# Revit family: Q90.195.xxx_with 3 shelves_4+6 drawers_RV15
name_source: partatom
category: Möbelsysteme
revit_build: Autodesk Revit 2015 (Build: 20140606_1530(x64)
units: mm (PartAtom-declared; Revit-internal decimal feet)

## types (27) — shared parameters
Beschreibung = GS-tested safety storage cabinets for unrestricted storage of flammable hazardous materials in work areas in accordance with EN 14470-1 and TRGS 510 with a fire resistance of 90 (Type 90)
Cabinet colour = RAL 7016 Anthracite grey
Cabinet depth = 615 mm  [stored 2.01772 ft]
Cabinet height = 1954 mm
Diff. pressure (Air change 10 times) = 5.0 Pa
Hersteller = asecos GmbH
Price information = Price from fall 2017
Price information 2 = Prices are ex works and without taxes and shipping
Product video = https://www.youtube.com
URL = https://www.asecos.com
zero-valued in all types: Sticker position rb

## per-type parameters (varying)
- Q90.195.060 with 3 shelves, warning yellow: 1200 mm 3 shelves=Nein; 1200 mm 4 drawers=Nein; 1200 mm 6 drawers=Nein; 600 mm 3 shelves=Ja; 600 mm 4 drawers=Nein; 600 mm 6 drawers=Nein; 900 mm 3 shelves=Nein; 900 mm 4 drawers=Nein; 900 mm 6 drawers=Nein; Air change 10 times=1.1 L/s; Air duct distance=145 mm  [stored 0.475722 ft]; Bestellnummer DACH=30072-040-30076; Cabinet width=600 mm; Distributed load=8.77 kN/m²; Door colour=RAL 1004 warning yellow; Door width=512 mm  [stored 1.67979 ft]; Double door=Nein; Handle position=514 mm; Kosten=2410 $; Modell=Q90.195.060 with 3 shelves; Order No. Global=30072-040-33407; Single door=Ja; Sticker position lb=269 mm; Sticker position ls=0 mm  [stored 0 ft]; Typenbild=30072-040.jpg
- Q90.195.060 with 3 shelves, light grey: 1200 mm 3 shelves=Nein; 1200 mm 4 drawers=Nein; 1200 mm 6 drawers=Nein; 600 mm 3 shelves=Ja; 600 mm 4 drawers=Nein; 600 mm 6 drawers=Nein; 900 mm 3 shelves=Nein; 900 mm 4 drawers=Nein; 900 mm 6 drawers=Nein; Air change 10 times=1.1 L/s; Air duct distance=145 mm  [stored 0.475722 ft]; Bestellnummer DACH=30072-041-30076; Cabinet width=600 mm; Distributed load=8.77 kN/m²; Door colour=RAL 7035 Light grey; Door width=512 mm  [stored 1.67979 ft]; Double door=Nein; Handle position=514 mm; Kosten=2410 $; Modell=Q90.195.060 with 3 shelves; Order No. Global=30072-041-33600; Single door=Ja; Sticker position lb=269 mm; Sticker position ls=0 mm  [stored 0 ft]; Typenbild=30072-041.jpg
- Q90.195.060 with 3 shelves, pure white: 1200 mm 3 shelves=Nein; 1200 mm 4 drawers=Nein; 1200 mm 6 drawers=Nein; 600 mm 3 shelves=Ja; 600 mm 4 drawers=Nein; 600 mm 6 drawers=Nein; 900 mm 3 shelves=Nein; 900 mm 4 drawers=Nein; 900 mm 6 drawers=Nein; Air change 10 times=1.1 L/s; Air duct distance=145 mm  [stored 0.475722 ft]; Bestellnummer DACH=30072-050-30076; Cabinet width=600 mm; Distributed load=8.77 kN/m²; Door colour=RAL 9010 Pure white; Door width=512 mm  [stored 1.67979 ft]; Double door=Nein; Handle position=514 mm; Kosten=2410 $; Modell=Q90.195.060 with 3 shelves; Order No. Global=30072-050-33407; Single door=Ja; Sticker position lb=269 mm; Sticker position ls=0 mm  [stored 0 ft]; Typenbild=30072-050.jpg
- Q90.195.060 with 4 drawers, warning yellow: 1200 mm 3 shelves=Nein; 1200 mm 4 drawers=Nein; 1200 mm 6 drawers=Nein; 600 mm 3 shelves=Nein; 600 mm 4 drawers=Ja; 600 mm 6 drawers=Nein; 900 mm 3 shelves=Nein; 900 mm 4 drawers=Nein; 900 mm 6 drawers=Nein; Air change 10 times=1.1 L/s; Air duct distance=145 mm  [stored 0.475722 ft]; Bestellnummer DACH=30072-040-30088; Cabinet width=600 mm; Distributed load=8.77 kN/m²; Door colour=RAL 1004 warning yellow; Door width=512 mm  [stored 1.67979 ft]; Double door=Nein; Handle position=514 mm; Kosten=2720 $; Modell=Q90.195.060 with 4 drawers; Order No. Global=30072-040-33608; Single door=Ja; Sticker position lb=269 mm; Sticker position ls=0 mm  [stored 0 ft]; Typenbild=30072-040.jpg
- Q90.195.060 with 4 drawers, light grey: 1200 mm 3 shelves=Nein; 1200 mm 4 drawers=Nein; 1200 mm 6 drawers=Nein; 600 mm 3 shelves=Nein; 600 mm 4 drawers=Ja; 600 mm 6 drawers=Nein; 900 mm 3 shelves=Nein; 900 mm 4 drawers=Nein; 900 mm 6 drawers=Nein; Air change 10 times=1.1 L/s; Air duct distance=145 mm  [stored 0.475722 ft]; Bestellnummer DACH=30072-041-30088; Cabinet width=600 mm; Distributed load=8.77 kN/m²; Door colour=RAL 7035 Light grey; Door width=512 mm  [stored 1.67979 ft]; Double door=Nein; Handle position=514 mm; Kosten=2720 $; Modell=Q90.195.060 with 4 drawers; Order No. Global=30072-041-333608; Single door=Ja; Sticker position lb=269 mm; Sticker position ls=0 mm  [stored 0 ft]; Typenbild=30072-041.jpg
- Q90.195.060 with 4 drawers, pure white: 1200 mm 3 shelves=Nein; 1200 mm 4 drawers=Nein; 1200 mm 6 drawers=Nein; 600 mm 3 shelves=Nein; 600 mm 4 drawers=Ja; 600 mm 6 drawers=Nein; 900 mm 3 shelves=Nein; 900 mm 4 drawers=Nein; 900 mm 6 drawers=Nein; Air change 10 times=1.1 L/s; Air duct distance=145 mm  [stored 0.475722 ft]; Bestellnummer DACH=30072-050-30088; Cabinet width=600 mm; Distributed load=8.77 kN/m²; Door colour=RAL 9010 Pure white; Door width=512 mm  [stored 1.67979 ft]; Double door=Nein; Handle position=514 mm; Kosten=2720 $; Modell=Q90.195.060 with 4 drawers; Order No. Global=30072-050-33608; Single door=Ja; Sticker position lb=269 mm; Sticker position ls=0 mm  [stored 0 ft]; Typenbild=30072-050.jpg
- Q90.195.060 with 6 drawers, warning yellow: 1200 mm 3 shelves=Nein; 1200 mm 4 drawers=Nein; 1200 mm 6 drawers=Nein; 600 mm 3 shelves=Nein; 600 mm 4 drawers=Nein; 600 mm 6 drawers=Ja; 900 mm 3 shelves=Nein; 900 mm 4 drawers=Nein; 900 mm 6 drawers=Nein; Air change 10 times=1.1 L/s; Air duct distance=145 mm  [stored 0.475722 ft]; Bestellnummer DACH=30072-040-30090; Cabinet width=600 mm; Distributed load=8.77 kN/m²; Door colour=RAL 1004 warning yellow; Door width=512 mm  [stored 1.67979 ft]; Double door=Nein; Handle position=514 mm; Kosten=2960 $; Modell=Q90.195.060 with 6 drawers; Order No. Global=30072-040-33610; Single door=Ja; Sticker position lb=269 mm; Sticker position ls=0 mm  [stored 0 ft]; Typenbild=30072-040.jpg
- Q90.195.060 with 6 drawers, light grey: 1200 mm 3 shelves=Nein; 1200 mm 4 drawers=Nein; 1200 mm 6 drawers=Nein; 600 mm 3 shelves=Nein; 600 mm 4 drawers=Nein; 600 mm 6 drawers=Ja; 900 mm 3 shelves=Nein; 900 mm 4 drawers=Nein; 900 mm 6 drawers=Nein; Air change 10 times=1.1 L/s; Air duct distance=145 mm  [stored 0.475722 ft]; Bestellnummer DACH=30072-041-30090; Cabinet width=600 mm; Distributed load=8.77 kN/m²; Door colour=RAL 7035 Light grey; Door width=512 mm  [stored 1.67979 ft]; Double door=Nein; Handle position=514 mm; Kosten=2960 $; Modell=Q90.195.060 with 6 drawers; Order No. Global=30072-041-33610; Single door=Ja; Sticker position lb=269 mm; Sticker position ls=0 mm  [stored 0 ft]; Typenbild=30072-041.jpg
- Q90.195.060 with 6 drawers, pure white: 1200 mm 3 shelves=Nein; 1200 mm 4 drawers=Nein; 1200 mm 6 drawers=Nein; 600 mm 3 shelves=Nein; 600 mm 4 drawers=Nein; 600 mm 6 drawers=Ja; 900 mm 3 shelves=Nein; 900 mm 4 drawers=Nein; 900 mm 6 drawers=Nein; Air change 10 times=1.1 L/s; Air duct distance=145 mm  [stored 0.475722 ft]; Bestellnummer DACH=30072-050-30090; Cabinet width=600 mm; Distributed load=8.77 kN/m²; Door colour=RAL 9010 Pure white; Door width=512 mm  [stored 1.67979 ft]; Double door=Nein; Handle position=514 mm; Kosten=2960 $; Modell=Q90.195.060 with 6 drawers; Order No. Global=30072-050-33610; Single door=Ja; Sticker position lb=269 mm; Sticker position ls=0 mm  [stored 0 ft]; Typenbild=30072-050.jpg
- Q90.195.090 with 3 shelves, warning yellow: 1200 mm 3 shelves=Nein; 1200 mm 4 drawers=Nein; 1200 mm 6 drawers=Nein; 600 mm 3 shelves=Nein; 600 mm 4 drawers=Nein; 600 mm 6 drawers=Nein; 900 mm 3 shelves=Ja; 900 mm 4 drawers=Nein; 900 mm 6 drawers=Nein; Air change 10 times=1.7 L/s; Air duct distance=292 mm  [stored 0.958005 ft]; Bestellnummer DACH=30041-040-30043; Cabinet width=894 mm; Distributed load=6.41 kN/m²; Door colour=RAL 1004 warning yellow; Door width=399 mm; Double door=Ja; Handle position=401 mm; Kosten=3000 $; Modell=Q90.195.090 with 3 shelves; Order No. Global=30041-040-33622; Single door=Nein; Sticker position lb=156 mm; Sticker position ls=300 mm; Typenbild=30041-040.jpg
- Q90.195.090 with 3 shelves, light grey: 1200 mm 3 shelves=Nein; 1200 mm 4 drawers=Nein; 1200 mm 6 drawers=Nein; 600 mm 3 shelves=Nein; 600 mm 4 drawers=Nein; 600 mm 6 drawers=Nein; 900 mm 3 shelves=Ja; 900 mm 4 drawers=Nein; 900 mm 6 drawers=Nein; Air change 10 times=1.7 L/s; Air duct distance=292 mm  [stored 0.958005 ft]; Bestellnummer DACH=30041-041-30043; Cabinet width=894 mm; Distributed load=6.41 kN/m²; Door colour=RAL 7035 Light grey; Door width=399 mm; Double door=Ja; Handle position=401 mm; Kosten=3000 $; Modell=Q90.195.090 with 3 shelves; Order No. Global=30041-041-33622; Single door=Nein; Sticker position lb=156 mm; Sticker position ls=300 mm; Typenbild=30041-041.jpg
- Q90.195.090 with 3 shelves, pure white: 1200 mm 3 shelves=Nein; 1200 mm 4 drawers=Nein; 1200 mm 6 drawers=Nein; 600 mm 3 shelves=Nein; 600 mm 4 drawers=Nein; 600 mm 6 drawers=Nein; 900 mm 3 shelves=Ja; 900 mm 4 drawers=Nein; 900 mm 6 drawers=Nein; Air change 10 times=1.7 L/s; Air duct distance=292 mm  [stored 0.958005 ft]; Bestellnummer DACH=30041-050-30043; Cabinet width=894 mm; Distributed load=6.41 kN/m²; Door colour=RAL 9010 Pure white; Door width=399 mm; Double door=Ja; Handle position=401 mm; Kosten=3000 $; Modell=Q90.195.090 with 3 shelves; Order No. Global=30041-050-33622; Single door=Nein; Sticker position lb=156 mm; Sticker position ls=300 mm; Typenbild=30041-050.jpg
- Q90.195.090 with 4 drawers, warning yellow: 1200 mm 3 shelves=Nein; 1200 mm 4 drawers=Nein; 1200 mm 6 drawers=Nein; 600 mm 3 shelves=Nein; 600 mm 4 drawers=Nein; 600 mm 6 drawers=Nein; 900 mm 3 shelves=Nein; 900 mm 4 drawers=Ja; 900 mm 6 drawers=Nein; Air change 10 times=1.7 L/s; Air duct distance=292 mm  [stored 0.958005 ft]; Bestellnummer DACH=30041-40-30053; Cabinet width=894 mm; Distributed load=6.41 kN/m²; Door colour=RAL 1004 warning yellow; Door width=399 mm; Double door=Ja; Handle position=401 mm; Kosten=3560 $; Modell=Q90.195.090 with 4 drawers; Order No. Global=30041-40-33627; Single door=Nein; Sticker position lb=156 mm; Sticker position ls=300 mm; Typenbild=30041-040.jpg
- Q90.195.090 with 4 drawers, light grey: 1200 mm 3 shelves=Nein; 1200 mm 4 drawers=Nein; 1200 mm 6 drawers=Nein; 600 mm 3 shelves=Nein; 600 mm 4 drawers=Nein; 600 mm 6 drawers=Nein; 900 mm 3 shelves=Nein; 900 mm 4 drawers=Ja; 900 mm 6 drawers=Nein; Air change 10 times=1.7 L/s; Air duct distance=292 mm  [stored 0.958005 ft]; Bestellnummer DACH=30041-41-30053; Cabinet width=894 mm; Distributed load=6.41 kN/m²; Door colour=RAL 7035 Light grey; Door width=399 mm; Double door=Ja; Handle position=401 mm; Kosten=3560 $; Modell=Q90.195.090 with 4 drawers; Order No. Global=30041-41-33627; Single door=Nein; Sticker position lb=156 mm; Sticker position ls=300 mm; Typenbild=30041-041.jpg
- Q90.195.090 with 4 drawers, pure white: 1200 mm 3 shelves=Nein; 1200 mm 4 drawers=Nein; 1200 mm 6 drawers=Nein; 600 mm 3 shelves=Nein; 600 mm 4 drawers=Nein; 600 mm 6 drawers=Nein; 900 mm 3 shelves=Nein; 900 mm 4 drawers=Ja; 900 mm 6 drawers=Nein; Air change 10 times=1.7 L/s; Air duct distance=292 mm  [stored 0.958005 ft]; Bestellnummer DACH=30041-050-30053; Cabinet width=894 mm; Distributed load=6.41 kN/m²; Door colour=RAL 9010 Pure white; Door width=399 mm; Double door=Ja; Handle position=401 mm; Kosten=3560 $; Modell=Q90.195.090 with 4 drawers; Order No. Global=30041-050-33627; Single door=Nein; Sticker position lb=156 mm; Sticker position ls=300 mm; Typenbild=30041-050.jpg
- Q90.195.090 with 6 drawers, warning yellow: 1200 mm 3 shelves=Nein; 1200 mm 4 drawers=Nein; 1200 mm 6 drawers=Nein; 600 mm 3 shelves=Nein; 600 mm 4 drawers=Nein; 600 mm 6 drawers=Nein; 900 mm 3 shelves=Nein; 900 mm 4 drawers=Nein; 900 mm 6 drawers=Ja; Air change 10 times=1.7 L/s; Air duct distance=292 mm  [stored 0.958005 ft]; Bestellnummer DACH=30041-040-30055; Cabinet width=894 mm; Distributed load=6.41 kN/m²; Door colour=RAL 1004 warning yellow; Door width=399 mm; Double door=Ja; Handle position=401 mm; Kosten=3940 $; Modell=Q90.195.090 with 6 drawers; Order No. Global=30041-040-33629; Single door=Nein; Sticker position lb=156 mm; Sticker position ls=300 mm; Typenbild=30041-040.jpg
- Q90.195.090 with 6 drawers, light grey: 1200 mm 3 shelves=Nein; 1200 mm 4 drawers=Nein; 1200 mm 6 drawers=Nein; 600 mm 3 shelves=Nein; 600 mm 4 drawers=Nein; 600 mm 6 drawers=Nein; 900 mm 3 shelves=Nein; 900 mm 4 drawers=Nein; 900 mm 6 drawers=Ja; Air change 10 times=1.7 L/s; Air duct distance=292 mm  [stored 0.958005 ft]; Bestellnummer DACH=30041-041-30055; Cabinet width=894 mm; Distributed load=6.41 kN/m²; Door colour=RAL 7035 Light grey; Door width=399 mm; Double door=Ja; Handle position=401 mm; Kosten=3940 $; Modell=Q90.195.090 with 6 drawers; Order No. Global=30041-041-33629; Single door=Nein; Sticker position lb=156 mm; Sticker position ls=300 mm; Typenbild=30041-041.jpg
- Q90.195.090 with 6 drawers, pure white: 1200 mm 3 shelves=Nein; 1200 mm 4 drawers=Nein; 1200 mm 6 drawers=Nein; 600 mm 3 shelves=Nein; 600 mm 4 drawers=Nein; 600 mm 6 drawers=Nein; 900 mm 3 shelves=Nein; 900 mm 4 drawers=Nein; 900 mm 6 drawers=Ja; Air change 10 times=1.7 L/s; Air duct distance=292 mm  [stored 0.958005 ft]; Bestellnummer DACH=30041-050-30055; Cabinet width=894 mm; Distributed load=6.41 kN/m²; Door colour=RAL 9010 Pure white; Door width=399 mm; Double door=Ja; Handle position=401 mm; Kosten=3940 $; Modell=Q90.195.090 with 6 drawers; Order No. Global=30041-050-33629; Single door=Nein; Sticker position lb=156 mm; Sticker position ls=300 mm; Typenbild=30041-050.jpg
- Q90.195.120 with 3 shelves, warning yellow: 1200 mm 3 shelves=Ja; 1200 mm 4 drawers=Nein; 1200 mm 6 drawers=Nein; 600 mm 3 shelves=Nein; 600 mm 4 drawers=Nein; 600 mm 6 drawers=Nein; 900 mm 3 shelves=Nein; 900 mm 4 drawers=Nein; 900 mm 6 drawers=Nein; Air change 10 times=2.5 L/s; Air duct distance=442 mm  [stored 1.45013 ft]; Bestellnummer DACH=30001-050-30003; Cabinet width=1194 mm; Distributed load=4.16 kN/m²; Door colour=RAL 1004 warning yellow; Door width=549 mm; Double door=Ja; Handle position=551 mm; Kosten=3340 $; Modell=Q90.195.120 with 3 shelves; Order No. Global=30001-050-33635; Single door=Nein; Sticker position lb=156 mm; Sticker position ls=450 mm  [stored 1.47638 ft]; Typenbild=30001-040.jpg
- Q90.195.120 with 3 shelves, light grey: 1200 mm 3 shelves=Ja; 1200 mm 4 drawers=Nein; 1200 mm 6 drawers=Nein; 600 mm 3 shelves=Nein; 600 mm 4 drawers=Nein; 600 mm 6 drawers=Nein; 900 mm 3 shelves=Nein; 900 mm 4 drawers=Nein; 900 mm 6 drawers=Nein; Air change 10 times=2.5 L/s; Air duct distance=442 mm  [stored 1.45013 ft]; Bestellnummer DACH=30001-041-30003; Cabinet width=1194 mm; Distributed load=4.16 kN/m²; Door colour=RAL 7035 Light grey; Door width=549 mm; Double door=Ja; Handle position=551 mm; Kosten=3340 $; Modell=Q90.195.120 with 3 shelves; Order No. Global=30001-041-33635; Single door=Nein; Sticker position lb=156 mm; Sticker position ls=450 mm  [stored 1.47638 ft]; Typenbild=30001-041.jpg
- Q90.195.120 with 3 shelves, pure white: 1200 mm 3 shelves=Ja; 1200 mm 4 drawers=Nein; 1200 mm 6 drawers=Nein; 600 mm 3 shelves=Nein; 600 mm 4 drawers=Nein; 600 mm 6 drawers=Nein; 900 mm 3 shelves=Nein; 900 mm 4 drawers=Nein; 900 mm 6 drawers=Nein; Air change 10 times=2.5 L/s; Air duct distance=442 mm  [stored 1.45013 ft]; Bestellnummer DACH=30001-050-30003; Cabinet width=1194 mm; Distributed load=4.16 kN/m²; Door colour=RAL 9010 Pure white; Door width=549 mm; Double door=Ja; Handle position=551 mm; Kosten=3340 $; Modell=Q90.195.120 with 3 shelves; Order No. Global=30001-050-33635; Single door=Nein; Sticker position lb=156 mm; Sticker position ls=450 mm  [stored 1.47638 ft]; Typenbild=30001-050.jpg
- Q90.195.120 with 4 drawers, warning yellow: 1200 mm 3 shelves=Nein; 1200 mm 4 drawers=Ja; 1200 mm 6 drawers=Nein; 600 mm 3 shelves=Nein; 600 mm 4 drawers=Nein; 600 mm 6 drawers=Nein; 900 mm 3 shelves=Nein; 900 mm 4 drawers=Nein; 900 mm 6 drawers=Nein; Air change 10 times=2.5 L/s; Air duct distance=442 mm  [stored 1.45013 ft]; Bestellnummer DACH=30001-040-30015; Cabinet width=1194 mm; Distributed load=4.16 kN/m²; Door colour=RAL 1004 warning yellow; Door width=549 mm; Double door=Ja; Handle position=551 mm; Kosten=3670 $; Modell=Q90.195.120 with 4 drawers; Order No. Global=30001-040-33647; Single door=Nein; Sticker position lb=156 mm; Sticker position ls=450 mm  [stored 1.47638 ft]; Typenbild=30001-040.jpg
- Q90.195.120 with 4 drawers, light grey: 1200 mm 3 shelves=Nein; 1200 mm 4 drawers=Ja; 1200 mm 6 drawers=Nein; 600 mm 3 shelves=Nein; 600 mm 4 drawers=Nein; 600 mm 6 drawers=Nein; 900 mm 3 shelves=Nein; 900 mm 4 drawers=Nein; 900 mm 6 drawers=Nein; Air change 10 times=2.5 L/s; Air duct distance=442 mm  [stored 1.45013 ft]; Bestellnummer DACH=30001-041-30015; Cabinet width=1194 mm; Distributed load=4.16 kN/m²; Door colour=RAL 7035 Light grey; Door width=549 mm; Double door=Ja; Handle position=551 mm; Kosten=3670 $; Modell=Q90.195.120 with 4 drawers; Order No. Global=30001-041-33647; Single door=Nein; Sticker position lb=156 mm; Sticker position ls=450 mm  [stored 1.47638 ft]; Typenbild=30001-041.jpg
- Q90.195.120 with 4 drawers, pure white: 1200 mm 3 shelves=Nein; 1200 mm 4 drawers=Ja; 1200 mm 6 drawers=Nein; 600 mm 3 shelves=Nein; 600 mm 4 drawers=Nein; 600 mm 6 drawers=Nein; 900 mm 3 shelves=Nein; 900 mm 4 drawers=Nein; 900 mm 6 drawers=Nein; Air change 10 times=2.5 L/s; Air duct distance=442 mm  [stored 1.45013 ft]; Bestellnummer DACH=30001-050-30015; Cabinet width=1194 mm; Distributed load=4.16 kN/m²; Door colour=RAL 9010 Pure white; Door width=549 mm; Double door=Ja; Handle position=551 mm; Kosten=3670 $; Modell=Q90.195.120 with 4 drawers; Order No. Global=30001-050-33647; Single door=Nein; Sticker position lb=156 mm; Sticker position ls=450 mm  [stored 1.47638 ft]; Typenbild=30001-050.jpg
- Q90.195.120 with 6 drawers, warning yellow: 1200 mm 3 shelves=Nein; 1200 mm 4 drawers=Nein; 1200 mm 6 drawers=Ja; 600 mm 3 shelves=Nein; 600 mm 4 drawers=Nein; 600 mm 6 drawers=Nein; 900 mm 3 shelves=Nein; 900 mm 4 drawers=Nein; 900 mm 6 drawers=Nein; Air change 10 times=2.5 L/s; Air duct distance=442 mm  [stored 1.45013 ft]; Bestellnummer DACH=30001-040-30017; Cabinet width=1194 mm; Distributed load=4.16 kN/m²; Door colour=RAL 1004 warning yellow; Door width=549 mm; Double door=Ja; Handle position=551 mm; Kosten=4050 $; Modell=Q90.195.120 with 6 drawers; Order No. Global=30001-040-33649; Single door=Nein; Sticker position lb=156 mm; Sticker position ls=450 mm  [stored 1.47638 ft]; Typenbild=30001-040.jpg
- Q90.195.120 with 6 drawers, light grey: 1200 mm 3 shelves=Nein; 1200 mm 4 drawers=Nein; 1200 mm 6 drawers=Ja; 600 mm 3 shelves=Nein; 600 mm 4 drawers=Nein; 600 mm 6 drawers=Nein; 900 mm 3 shelves=Nein; 900 mm 4 drawers=Nein; 900 mm 6 drawers=Nein; Air change 10 times=2.5 L/s; Air duct distance=442 mm  [stored 1.45013 ft]; Bestellnummer DACH=30001-041-30017; Cabinet width=1194 mm; Distributed load=4.16 kN/m²; Door colour=RAL 7035 Light grey; Door width=549 mm; Double door=Ja; Handle position=551 mm; Kosten=4050 $; Modell=Q90.195.120 with 6 drawers; Order No. Global=30001-041-33649; Single door=Nein; Sticker position lb=156 mm; Sticker position ls=450 mm  [stored 1.47638 ft]; Typenbild=30001-041.jpg
- Q90.195.120 with 6 drawers, pure white: 1200 mm 3 shelves=Nein; 1200 mm 4 drawers=Nein; 1200 mm 6 drawers=Ja; 600 mm 3 shelves=Nein; 600 mm 4 drawers=Nein; 600 mm 6 drawers=Nein; 900 mm 3 shelves=Nein; 900 mm 4 drawers=Nein; 900 mm 6 drawers=Nein; Air change 10 times=2.5 L/s; Air duct distance=442 mm  [stored 1.45013 ft]; Bestellnummer DACH=30001-050-30017; Cabinet width=1194 mm; Distributed load=4.16 kN/m²; Door colour=RAL 9010 Pure white; Door width=549 mm; Double door=Ja; Handle position=551 mm; Kosten=4050 $; Modell=Q90.195.120 with 6 drawers; Order No. Global=30001-050-33649; Single door=Nein; Sticker position lb=156 mm; Sticker position ls=450 mm  [stored 1.47638 ft]; Typenbild=30001-050.jpg

note: [stored X ft] marks values corroborated as IEEE doubles in the binary element streams (Revit-internal decimal feet)
